FCSTD DOCUMENT  (FreeCAD 0.15R4237 (Git))
Label: Sliding 2-panes window
License: CC-BY 3.0
LicenseURL: http://creativecommons.org/licenses/by/3.0/
objects: Sketcher::SketchObject×1, Part::FeaturePython×1
note: 3 computed .brp shape members not serialized (recipe doc carries the construction recipe); baked Part::Feature solids carry a one-line shape summary decoded from their .brp

FEATURE [Sketcher::SketchObject] Sketch  label="Sketch2Coulissants"
  Placement = pos=(0,0,0) rot=(1,0,0;1.5708rad)
  sketch-geometry (24):
    g0: LineSegment StartX=0 StartY=0 StartZ=0 EndX=2000 EndY=0 EndZ=0
    g1: LineSegment StartX=2000 StartY=0 StartZ=0 EndX=2000 EndY=2200 EndZ=0
    g2: LineSegment StartX=2000 StartY=2200 StartZ=0 EndX=0 EndY=2200 EndZ=0
    g3: LineSegment StartX=0 StartY=2200 StartZ=0 EndX=0 EndY=0 EndZ=0
    g4: LineSegment StartX=50 StartY=50 StartZ=0 EndX=1950 EndY=50 EndZ=0
    g5: LineSegment StartX=1950 StartY=50 StartZ=0 EndX=1950 EndY=2150 EndZ=0
    g6: LineSegment StartX=1950 StartY=2150 StartZ=0 EndX=50 EndY=2150 EndZ=0
    g7: LineSegment StartX=50 StartY=2150 StartZ=0 EndX=50 EndY=50 EndZ=0
    g8: LineSegment StartX=55 StartY=55 StartZ=0 EndX=1035 EndY=55 EndZ=0
    g9: LineSegment StartX=1035 StartY=55 StartZ=0 EndX=1035 EndY=2145 EndZ=0
    g10: LineSegment StartX=1035 StartY=2145 StartZ=0 EndX=55 EndY=2145 EndZ=0
    g11: LineSegment StartX=55 StartY=2145 StartZ=0 EndX=55 EndY=55 EndZ=0
    g12: LineSegment StartX=105 StartY=105 StartZ=0 EndX=965 EndY=105 EndZ=0
    g13: LineSegment StartX=965 StartY=105 StartZ=0 EndX=965 EndY=2095 EndZ=0
    g14: LineSegment StartX=965 StartY=2095 StartZ=0 EndX=105 EndY=2095 EndZ=0
    g15: LineSegment StartX=105 StartY=2095 StartZ=0 EndX=105 EndY=105 EndZ=0
    g16: LineSegment StartX=965 StartY=55 StartZ=0 EndX=1945 EndY=55 EndZ=0
    g17: LineSegment StartX=1945 StartY=55 StartZ=0 EndX=1945 EndY=2145 EndZ=0
    g18: LineSegment StartX=1945 StartY=2145 StartZ=0 EndX=965 EndY=2145 EndZ=0
    g19: LineSegment StartX=965 StartY=2145 StartZ=0 EndX=965 EndY=55 EndZ=0
    g20: LineSegment StartX=1035 StartY=105 StartZ=0 EndX=1895 EndY=105 EndZ=0
    g21: LineSegment StartX=1895 StartY=105 StartZ=0 EndX=1895 EndY=2095 EndZ=0
    g22: LineSegment StartX=1895 StartY=2095 StartZ=0 EndX=1035 EndY=2095 EndZ=0
    g23: LineSegment StartX=1035 StartY=2095 StartZ=0 EndX=1035 EndY=105 EndZ=0
  constraints (71):
    c: Coincident(g0,g1)
    c: Coincident(g1,g2)
    c: Coincident(g2,g3)
    c: Coincident(g3,g0)
    c: Horizontal(g0)
    c: Horizontal(g2)
    c: Vertical(g1)
    c: Vertical(g3)
    c: Coincident(g4,g5)
    c: Coincident(g5,g6)
    c: Coincident(g6,g7)
    c: Coincident(g7,g4)
    c: Horizontal(g4)
    c: Horizontal(g6)
    c: Vertical(g5)
    c: Vertical(g7)
    c: DistanceY(g1) = 2200
    c: DistanceX(g0) = 2000
    c: DistanceY(g6,g2) = 50
    c: DistanceX(g2,g6) = 50
    c: DistanceX(g4,g0) = 50
    c: DistanceY(g0,g4) = 50
    c: Coincident(g0,g-1)
    c: Coincident(g8,g9)
    c: Coincident(g9,g10)
    c: Coincident(g10,g11)
    c: Coincident(g11,g8)
    c: Horizontal(g8)
    c: Horizontal(g10)
    c: Vertical(g9)
    c: Vertical(g11)
    c: Coincident(g12,g13)
    c: Coincident(g13,g14)
    c: Coincident(g14,g15)
    c: Coincident(g15,g12)
    c: Horizontal(g12)
    c: Horizontal(g14)
    c: Vertical(g13)
    c: Vertical(g15)
    c: Coincident(g16,g17)
    c: Coincident(g17,g18)
    c: Coincident(g18,g19)
    c: Coincident(g19,g16)
    c: Horizontal(g16)
    c: Horizontal(g18)
    c: Vertical(g17)
    c: Vertical(g19)
    c: Coincident(g20,g21)
    c: Coincident(g21,g22)
    c: Coincident(g22,g23)
    c: Coincident(g23,g20)
    c: Horizontal(g20)
    c: Horizontal(g22)
    c: Vertical(g21)
    c: Vertical(g23)
    c: DistanceY(g8,g12) = 50
    c: DistanceX(g8,g12) = 50
    c: DistanceX(g21,g17) = 50
    c: DistanceY(g21,g17) = 50
    c: DistanceX(g14,g10) = 70
    c: DistanceY(g8,g16) = 0
    c: DistanceY(g10,g18) = 0
    c: DistanceX(g4,g8) = 5
    c: DistanceY(g4,g8) = 5
    c: DistanceX(g6,g18) = -5
    c: DistanceY(g6,g18) = -5
    c: PointOnObject(g13,g22)
    c: PointOnObject(g20,g12)
    c: PointOnObject(g13,g19)
    c: PointOnObject(g22,g9)
    c: Equal(g22,g14)
FEATURE [Part::FeaturePython] Fen__tre  label="Fenetre2Coulissants"  # WARN: FeaturePython — macro-defined, semantics opaque (R4)
  Base = -> Sketch
  Height = 2200
  HoleDepth = 0
  Normal = (0,1,0)
  Preset = 5
  Role = 0
  Width = 2000
  WindowParts = OuterFrame | Frame | Wire0,Wire1 | 100.0 | 0.0 | LeftFrame | Frame | Wire2,Wire3 | 30.0 | 40.0 | LeftGlass | Glass panel | Wire3 | 10.0 | 50.0 | RightFrame | Frame | Wire4,Wire5 | 30.0 | 70.0 | RightGlass | Glass panel | Wire5 | 10.0 | 80.0
